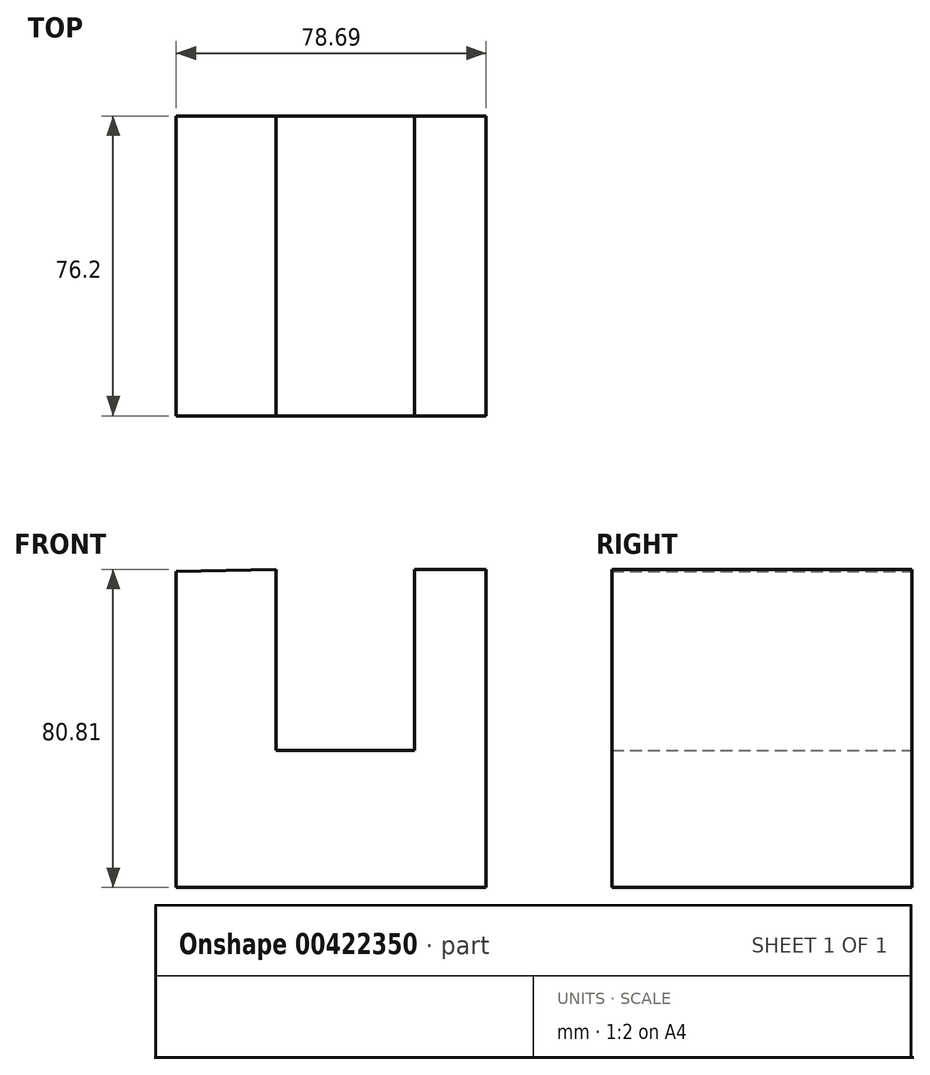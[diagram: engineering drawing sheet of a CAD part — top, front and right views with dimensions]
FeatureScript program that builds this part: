
annotation { "Feature Type Name" : "Feature", "Feature Type Description" : "" }
export const myFeature = defineFeature(function(context is Context, id is Id, definition is map)
    precondition{}
    {
        {
            var Q0;
            Q0=qCreatedBy(makeId("Front.planeOp"),FACE);
            var sketch = newSketch(context, id + "F0", { "sketchPlane" : qUnion([Q0])});
            skLineSegment(sketch, "E0", {"start": v(-33.8, 38.29) * mm, "end": v(-33.8, -41.99) * mm});
            skLineSegment(sketch, "E1", {"start": v(-33.8, -41.99) * mm, "end": v(44.9, -41.99) * mm});
            skLineSegment(sketch, "E2", {"start": v(44.9, -41.99) * mm, "end": v(44.9, 38.82) * mm});
            skLineSegment(sketch, "E3", {"start": v(44.9, 38.82) * mm, "end": v(26.67, 38.82) * mm});
            skLineSegment(sketch, "E4", {"start": v(26.67, 38.82) * mm, "end": v(26.67, -7.13) * mm});
            skLineSegment(sketch, "E5", {"start": v(26.67, -7.13) * mm, "end": v(-8.45, -7.13) * mm});
            skLineSegment(sketch, "E6", {"start": v(-8.45, -7.13) * mm, "end": v(-8.45, 38.82) * mm});
            skLineSegment(sketch, "E7", {"start": v(-8.45, 38.82) * mm, "end": v(-33.8, 38.29) * mm});
            skSolve(sketch);
        }
        {
            var Q0;
            Q0 = qSketchRegion(id + "F0", true);
            extrude(context, id + "F1", {"entities" : qUnion([Q0]), "depth" : 76.2 * mm});
        }
    });
